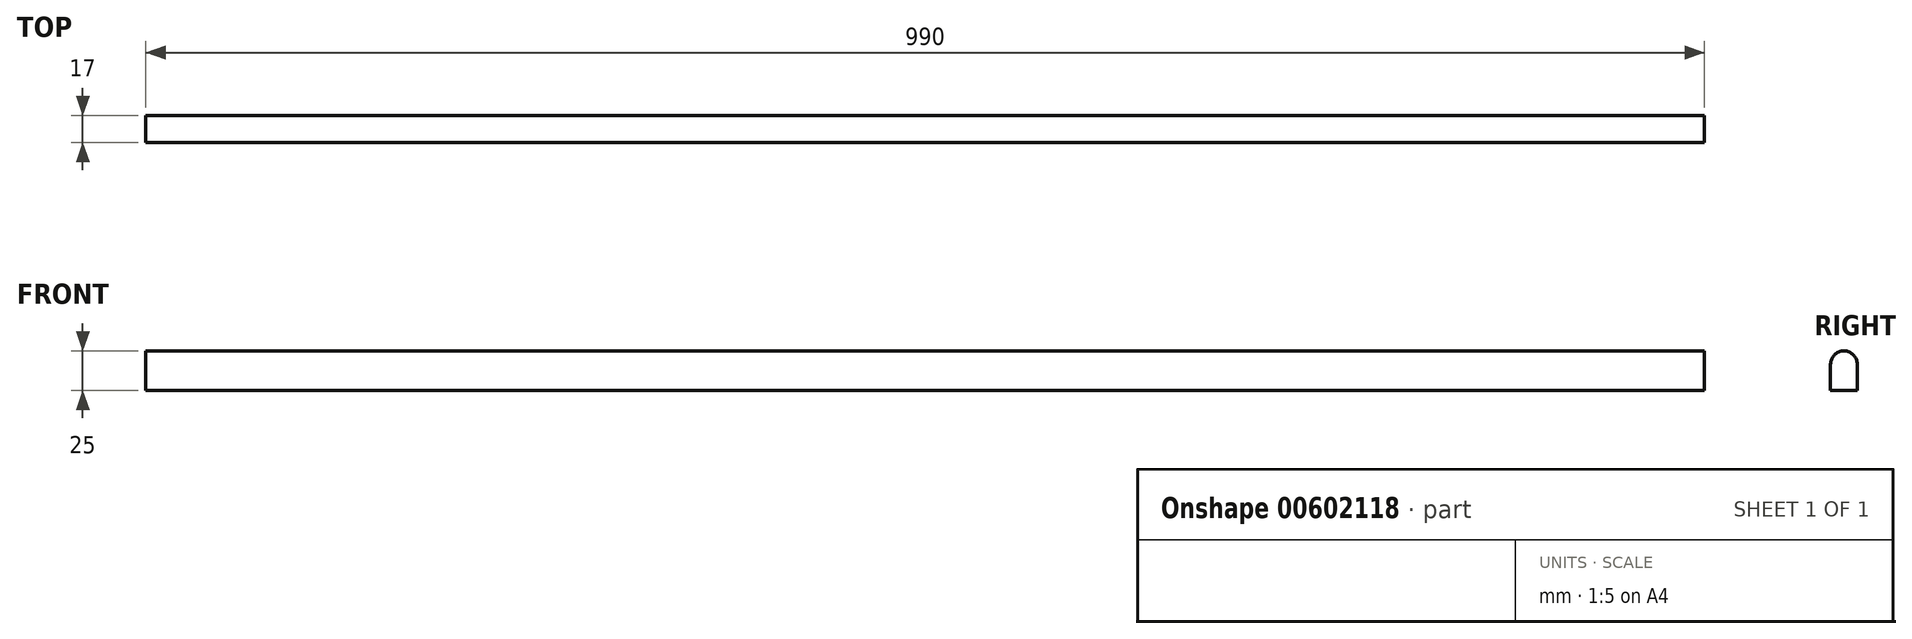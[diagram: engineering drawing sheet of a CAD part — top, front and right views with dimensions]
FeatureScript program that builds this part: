
annotation { "Feature Type Name" : "Feature", "Feature Type Description" : "" }
export const myFeature = defineFeature(function(context is Context, id is Id, definition is map)
    precondition{}
    {
        {
            var Q0;
            Q0=qCreatedBy(makeId("Right.planeOp"),FACE);
            var sketch = newSketch(context, id + "F0", { "sketchPlane" : qUnion([Q0])});
            skArc(sketch, "E0", {"start": v(8.5, 16.5) * mm, "mid": v(0, 25) * mm, "end": v(-8.5, 16.5) * mm});
            skLineSegment(sketch, "E1", {"start": v(8.5, 16.5) * mm, "end": v(8.5, 0) * mm});
            skLineSegment(sketch, "E2", {"start": v(-8.5, 16.5) * mm, "end": v(-8.5, 0) * mm});
            skLineSegment(sketch, "E3", {"start": v(-8.5, 0) * mm, "end": v(8.5, 0) * mm});
            skSolve(sketch);
        }
        {
            var Q0;
            Q0 = qSketchRegion(id + "F0", true);
            extrude(context, id + "F1", {"entities" : qUnion([Q0]), "depth" : 990 * mm, "offsetDistance" : 25 * mm});
        }
    });
